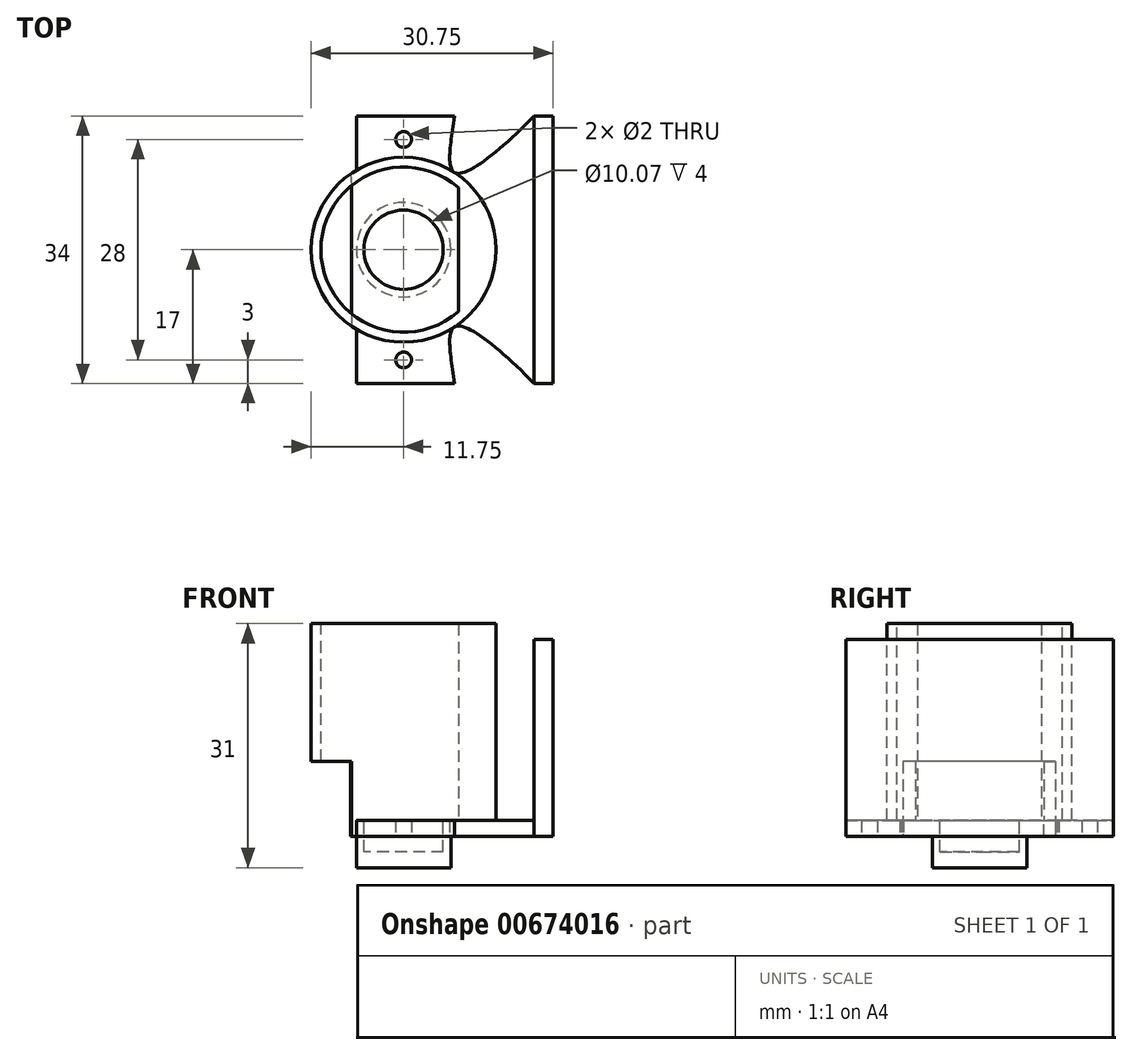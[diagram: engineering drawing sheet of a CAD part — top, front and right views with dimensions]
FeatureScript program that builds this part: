
annotation { "Feature Type Name" : "Feature", "Feature Type Description" : "" }
export const myFeature = defineFeature(function(context is Context, id is Id, definition is map)
    precondition{}
    {
        {
            var Q0;
            Q0=qCreatedBy(makeId("Top.planeOp"),FACE);
            var sketch = newSketch(context, id + "F0", { "sketchPlane" : qUnion([Q0])});
            skLineSegment(sketch, "E0", {"start": v(0, 0) * mm, "end": v(-6.62, 0) * mm});
            skLineSegment(sketch, "E1", {"start": v(-6.62, 0) * mm, "end": v(-6.62, 8.15) * mm});
            skLineSegment(sketch, "E2", {"start": v(-6.62, 0) * mm, "end": v(-6.62, -8.15) * mm});
            skLineSegment(sketch, "E3", {"start": v(6.95, -7.87) * mm, "end": v(6.95, 7.87) * mm});
            skArc(sketch, "E4", {"start": v(-6.62, 8.15) * mm, "mid": v(-10.5, 0) * mm, "end": v(-6.62, -8.15) * mm});
            skArc(sketch, "E5", {"start": v(6.95, 7.87) * mm, "mid": v(0.22, 10.5) * mm, "end": v(-6.62, 8.15) * mm});
            skArc(sketch, "E6", {"start": v(-6.62, -8.15) * mm, "mid": v(0.22, -10.5) * mm, "end": v(6.95, -7.87) * mm});
            skArc(sketch, "E7", {"start": v(6.95, -7.87) * mm, "mid": v(10.5, 0) * mm, "end": v(6.95, 7.87) * mm});
            skCircle(sketch, "E8", {"center": v(0, 0) * mm, "radius": 11.75 * mm});
            skCircle(sketch, "E9", {"center": v(0, 0) * mm, "radius": 6 * mm});
            skCircle(sketch, "E10", {"center": v(0, 0) * mm, "radius": 5.04 * mm});
            skLineSegment(sketch, "E11", {"start": v(-6.62, -8.15) * mm, "end": v(-6.62, -9.7) * mm});
            skLineSegment(sketch, "E12", {"start": v(-6.62, 8.15) * mm, "end": v(-6.73, 9.63) * mm});
            skSolve(sketch);
        }
        {
            var Q0;
            Q0=makeQuery(id+"F0.imprint","IMPRINT",FACE,{"disambiguationData":[TD([[makeQuery(id+"F0.imprint","IMPRINT",EDGE,{"derivedFrom":sQuery(id+"F0.wireOp",EDGE,"E5")}),-1.0]])]});
            var Q1;
            Q1=makeQuery(id+"F0.imprint","IMPRINT",FACE,{"disambiguationData":[TD([[makeQuery(id+"F0.imprint","IMPRINT",EDGE,{"derivedFrom":sQuery(id+"F0.wireOp",EDGE,"E4")}),-1.0]])]});
            var Q2;
            Q2=makeQuery(id+"F0.imprint","IMPRINT",FACE,{"disambiguationData":[TD([[makeQuery(id+"F0.imprint","IMPRINT",EDGE,{"derivedFrom":sQuery(id+"F0.wireOp",EDGE,"E1")}),-1.0]])]});
            var Q3;
            Q3=makeQuery(id+"F0.imprint","IMPRINT",FACE,{"disambiguationData":[TD([[makeQuery(id+"F0.imprint","IMPRINT",EDGE,{"derivedFrom":sQuery(id+"F0.wireOp",EDGE,"E9")}),1.0]])]});
            var Q4;
            Q4=makeQuery(id+"F0.imprint","IMPRINT",FACE,{"disambiguationData":[TD([[makeQuery(id+"F0.imprint","IMPRINT",EDGE,{"derivedFrom":sQuery(id+"F0.wireOp",EDGE,"E10")}),1.0]])]});
            var Q5;
            Q5=makeQuery(id+"F0.imprint","IMPRINT",FACE,{"disambiguationData":[TD([[makeQuery(id+"F0.imprint","IMPRINT",EDGE,{"derivedFrom":sQuery(id+"F0.wireOp",EDGE,"E3")}),-1.0]])]});
            extrude(context, id + "F1", {"entities" : qUnion([Q0, Q1, Q2, Q3, Q4, Q5]), "oppositeDirection" : true, "depth" : 2 * mm, "offsetDistance" : 25 * mm});
        }
        {
            var Q0;
            Q0=makeQuery(id+"F0.imprint","IMPRINT",FACE,{"disambiguationData":[TD([[makeQuery(id+"F0.imprint","IMPRINT",EDGE,{"derivedFrom":sQuery(id+"F0.wireOp",EDGE,"E5")}),-1.0]])]});
            var Q1;
            Q1=makeQuery(id+"F0.imprint","IMPRINT",FACE,{"disambiguationData":[TD([[makeQuery(id+"F0.imprint","IMPRINT",EDGE,{"derivedFrom":sQuery(id+"F0.wireOp",EDGE,"E4")}),-1.0]])]});
            var Q2;
            Q2=makeQuery(id+"F0.imprint","IMPRINT",FACE,{"disambiguationData":[TD([[makeQuery(id+"F0.imprint","IMPRINT",EDGE,{"derivedFrom":sQuery(id+"F0.wireOp",EDGE,"E3")}),-1.0]])]});
            extrude(context, id + "F2", {"entities" : qUnion([Q0, Q1, Q2]), "operationType" : NewBodyOperationType.ADD, "depth" : 25 * mm, "offsetDistance" : 25 * mm});
        }
        {
            var Q0;
            Q0=makeQuery(id+"F0.imprint","IMPRINT",FACE,{"disambiguationData":[TD([[makeQuery(id+"F0.imprint","IMPRINT",EDGE,{"derivedFrom":sQuery(id+"F0.wireOp",EDGE,"E9")}),1.0]])]});
            var Q1;
            Q1=makeQuery(id+"F0.imprint","IMPRINT",FACE,{"disambiguationData":[TD([[makeQuery(id+"F0.imprint","IMPRINT",EDGE,{"derivedFrom":sQuery(id+"F0.wireOp",EDGE,"E10")}),1.0]])]});
            extrude(context, id + "F3", {"entities" : qUnion([Q0, Q1]), "operationType" : NewBodyOperationType.ADD, "oppositeDirection" : true, "depth" : 6 * mm, "offsetDistance" : 25 * mm});
        }
        {
            var Q0;
            Q0=makeQuery(id+"F0.imprint","IMPRINT",FACE,{"disambiguationData":[TD([[makeQuery(id+"F0.imprint","IMPRINT",EDGE,{"derivedFrom":sQuery(id+"F0.wireOp",EDGE,"E10")}),1.0]])]});
            extrude(context, id + "F4", {"entities" : qUnion([Q0]), "operationType" : NewBodyOperationType.REMOVE, "oppositeDirection" : true, "depth" : 4 * mm, "offsetDistance" : 25 * mm});
        }
        {
            var Q0;
            Q0=makeQuery(id+"F0.imprint","IMPRINT",FACE,{"disambiguationData":[TD([[makeQuery(id+"F0.imprint","IMPRINT",EDGE,{"derivedFrom":sQuery(id+"F0.wireOp",EDGE,"E4")}),-1.0]])]});
            extrude(context, id + "F5", {"entities" : qUnion([Q0]), "operationType" : NewBodyOperationType.REMOVE, "depth" : 15 * mm, "offsetDistance" : 25 * mm, "symmetric" : true});
        }
        {
            var Q0;
            Q0=makeQuery(id+"F1.opExtrude","CAP_FACE",FACE,{"disambiguationData":[OSD([sQuery(id+"F0.wireOp",EDGE,"E1"),sQuery(id+"F0.wireOp",EDGE,"E2"),sQuery(id+"F0.wireOp",EDGE,"E4"),sQuery(id+"F0.wireOp",EDGE,"E8")])],"isStart":false});
            var sketch = newSketch(context, id + "F6", { "sketchPlane" : qUnion([Q0])});
            skCircle(sketch, "E13", {"center": v(0, 0) * mm, "radius": 6 * mm});
            skLineSegment(sketch, "E14", {"start": v(-6, 0) * mm, "end": v(-6, 17) * mm});
            skLineSegment(sketch, "E15", {"start": v(-6, 0) * mm, "end": v(-6, -17) * mm});
            skLineSegment(sketch, "E16", {"start": v(-6, -17) * mm, "end": v(19, -17) * mm});
            skLineSegment(sketch, "E17", {"start": v(-6, 17) * mm, "end": v(19, 17) * mm});
            skLineSegment(sketch, "E18", {"start": v(19, -17) * mm, "end": v(19, 17) * mm});
            skLineSegment(sketch, "E19", {"start": v(19, -17) * mm, "end": v(16.59, -17) * mm});
            skLineSegment(sketch, "E20", {"start": v(16.59, -17) * mm, "end": v(16.59, 17) * mm});
            skLineSegment(sketch, "E21", {"start": v(0, 0) * mm, "end": v(0, 14) * mm});
            skLineSegment(sketch, "E22", {"start": v(0, 0) * mm, "end": v(0, -14) * mm});
            skPoint(sketch, "E23.1.internal.snap0", {"position": v(6.5, -17) * mm});
            skFitSpline(sketch, "E23", {"points": [v(6.5, -17) * mm, v(6.5, -9.79) * mm, v(16.59, -17) * mm], "startDerivative": vector(-4, 25.58) * mm, "endDerivative": vector(23.12, -23.66) * mm});
            skPoint(sketch, "E24.1.internal.snap0", {"position": v(6.5, 17) * mm});
            skFitSpline(sketch, "E24", {"points": [v(6.5, 17) * mm, v(6.5, 9.79) * mm, v(16.59, 17) * mm], "startDerivative": vector(-4, -25.58) * mm, "endDerivative": vector(23.12, 23.66) * mm});
            skPoint(sketch, "E25", {"position": v(0, -14) * mm});
            skPoint(sketch, "E26", {"position": v(0, 14) * mm});
            skCircle(sketch, "E27", {"center": v(0, -14) * mm, "radius": 1 * mm});
            skCircle(sketch, "E28", {"center": v(0, 14) * mm, "radius": 1 * mm});
            skSolve(sketch);
        }
        {
            var Q0;
            {var subQ0=sQuery(id+"F6.wireOp",EDGE,"E20");Q0=makeQuery(id+"F6.imprint","IMPRINT",FACE,{"disambiguationData":[TD([[makeQuery(id+"F6.imprint","IMPRINT",EDGE,{"derivedFrom":subQ0}),1.0]])]});}
            var Q1;
            {var subQ0=sQuery(id+"F6.wireOp",EDGE,"E15");var subQ5=sQuery(id+"F6.wireOp",EDGE,"E16");var subQ8=makeQuery(id+"F6.imprint","INTERSECT",VERTEX,{"derivedFrom":[subQ0,subQ5]});Q1=makeQuery(id+"F6.imprint","IMPRINT",FACE,{"disambiguationData":[TD([[makeQuery(id+"F6.imprint","IMPRINT",EDGE,{"disambiguationData":[TD([[subQ8,1.0]])],"derivedFrom":subQ0}),1.0]])]});}
            var Q2;
            {var subQ1=sQuery(id+"F6.wireOp",EDGE,"E17");var subQ5=sQuery(id+"F6.wireOp",EDGE,"E14");var subQ8=makeQuery(id+"F6.imprint","INTERSECT",VERTEX,{"derivedFrom":[subQ5,subQ1]});Q2=makeQuery(id+"F6.imprint","IMPRINT",FACE,{"disambiguationData":[TD([[makeQuery(id+"F6.imprint","IMPRINT",EDGE,{"disambiguationData":[TD([[subQ8,1.0]])],"derivedFrom":subQ5}),-1.0]])]});}
            var Q3;
            {var subQ0=sQuery(id+"F6.wireOp",EDGE,"E18");Q3=makeQuery(id+"F6.imprint","IMPRINT",FACE,{"disambiguationData":[TD([[makeQuery(id+"F6.imprint","IMPRINT",EDGE,{"derivedFrom":subQ0}),1.0]])]});}
            extrude(context, id + "F7", {"entities" : qUnion([Q0, Q1, Q2, Q3]), "operationType" : NewBodyOperationType.ADD, "oppositeDirection" : true, "depth" : 2 * mm, "offsetDistance" : 25 * mm});
        }
        {
            var Q0;
            {var subQ0=sQuery(id+"F6.wireOp",EDGE,"E18");Q0=makeQuery(id+"F6.imprint","IMPRINT",FACE,{"disambiguationData":[TD([[makeQuery(id+"F6.imprint","IMPRINT",EDGE,{"derivedFrom":subQ0}),1.0]])]});}
            extrude(context, id + "F8", {"entities" : qUnion([Q0]), "operationType" : NewBodyOperationType.ADD, "oppositeDirection" : true, "depth" : 25 * mm, "offsetDistance" : 25 * mm});
        }
    });
